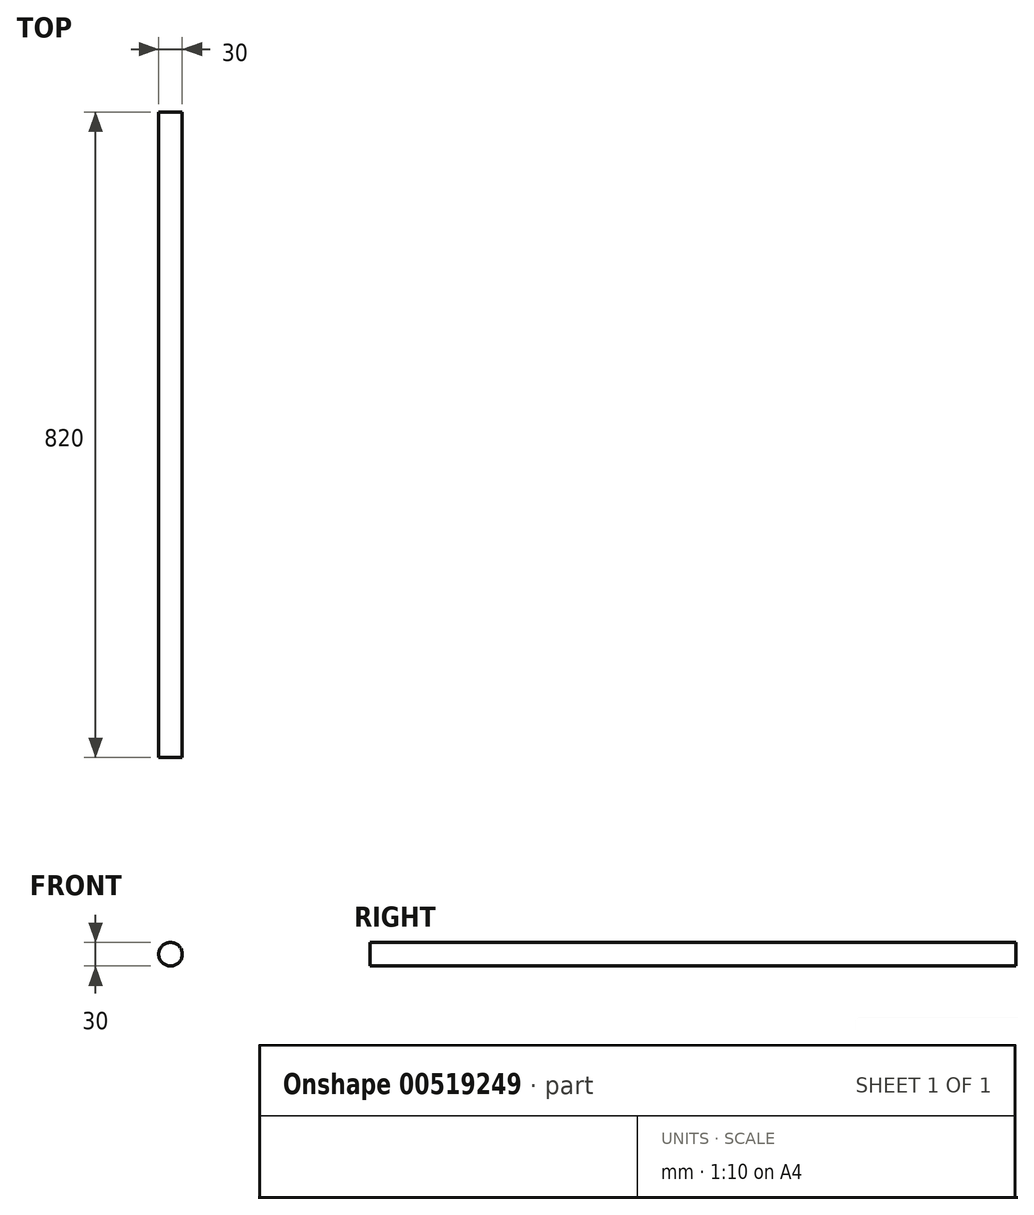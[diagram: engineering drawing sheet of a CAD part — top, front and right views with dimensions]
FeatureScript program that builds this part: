
annotation { "Feature Type Name" : "Feature", "Feature Type Description" : "" }
export const myFeature = defineFeature(function(context is Context, id is Id, definition is map)
    precondition{}
    {
        {
            var Q0;
            Q0=qCreatedBy(makeId("Front.planeOp"),FACE);
            var sketch = newSketch(context, id + "F0", { "sketchPlane" : qUnion([Q0])});
            skCircle(sketch, "E0", {"center": v(0, 0) * mm, "radius": 15 * mm});
            skSolve(sketch);
        }
        {
            var Q0;
            Q0 = qSketchRegion(id + "F0", true);
            extrude(context, id + "F1", {"entities" : qUnion([Q0]), "depth" : 820 * mm, "offsetDistance" : 25 * mm});
        }
    });
